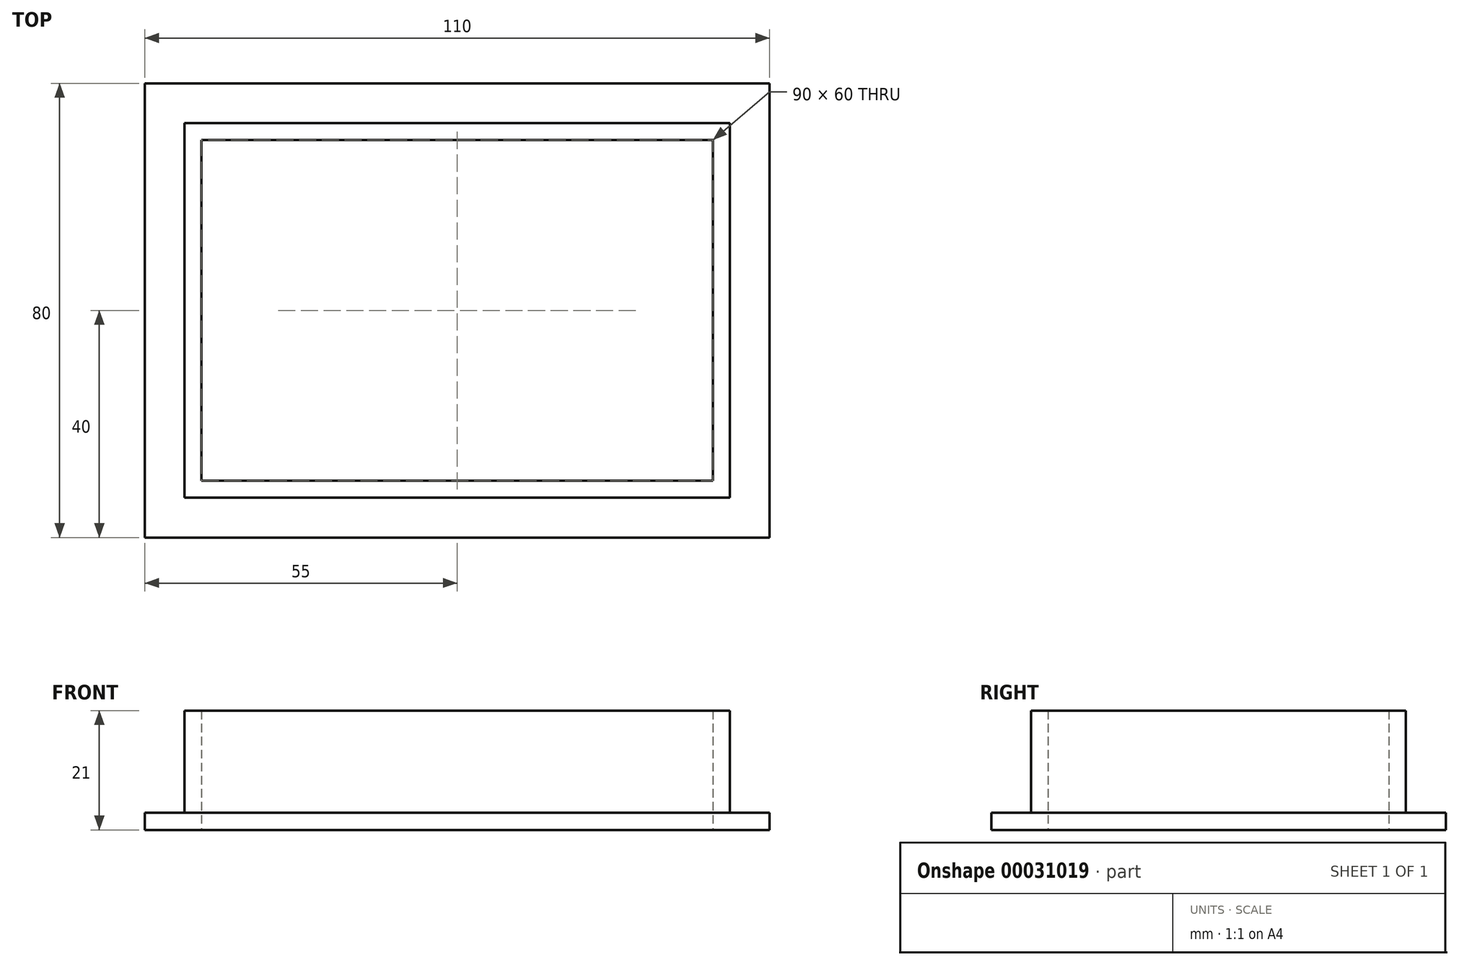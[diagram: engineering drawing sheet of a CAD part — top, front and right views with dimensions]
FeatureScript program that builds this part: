
annotation { "Feature Type Name" : "Feature", "Feature Type Description" : "" }
export const myFeature = defineFeature(function(context is Context, id is Id, definition is map)
    precondition{}
    {
        {
            var Q0;
            Q0=qCreatedBy(makeId("Top.planeOp"),FACE);
            var sketch = newSketch(context, id + "F0", { "sketchPlane" : qUnion([Q0])});
            skLineSegment(sketch, "E0.bottom", {"start": v(0, 0) * mm, "end": v(110, 0) * mm});
            skLineSegment(sketch, "E0.top", {"start": v(0, 80) * mm, "end": v(110, 80) * mm});
            skLineSegment(sketch, "E0.left", {"start": v(0, 0) * mm, "end": v(0, 80) * mm});
            skLineSegment(sketch, "E0.right", {"start": v(110, 0) * mm, "end": v(110, 80) * mm});
            skLineSegment(sketch, "E1.bottom", {"start": v(10, 10) * mm, "end": v(100, 10) * mm});
            skLineSegment(sketch, "E1.top", {"start": v(10, 70) * mm, "end": v(100, 70) * mm});
            skLineSegment(sketch, "E1.left", {"start": v(10, 10) * mm, "end": v(10, 70) * mm});
            skLineSegment(sketch, "E1.right", {"start": v(100, 10) * mm, "end": v(100, 70) * mm});
            skSolve(sketch);
        }
        {
            var Q0;
            Q0=makeQuery(id+"F0.imprint","IMPRINT",FACE,{"disambiguationData":[TD([[makeQuery(id+"F0.imprint","IMPRINT",EDGE,{"derivedFrom":sQuery(id+"F0.wireOp",EDGE,"E0.bottom")}),1.0]])]});
            extrude(context, id + "F1", {"entities" : qUnion([Q0]), "depth" : 3 * mm});
        }
        {
            var Q0;
            Q0=makeQuery(id+"F1.opExtrude","CAP_FACE",FACE,{"disambiguationData":[OSD([sQuery(id+"F0.wireOp",EDGE,"E0.bottom"),sQuery(id+"F0.wireOp",EDGE,"E0.top"),sQuery(id+"F0.wireOp",EDGE,"E0.left"),sQuery(id+"F0.wireOp",EDGE,"E0.right"),sQuery(id+"F0.wireOp",EDGE,"E1.bottom"),sQuery(id+"F0.wireOp",EDGE,"E1.top"),sQuery(id+"F0.wireOp",EDGE,"E1.left"),sQuery(id+"F0.wireOp",EDGE,"E1.right")])],"isStart":false});
            var sketch = newSketch(context, id + "F2", { "sketchPlane" : qUnion([Q0])});
            skLineSegment(sketch, "E2.bottom", {"start": v(7, 73) * mm, "end": v(103, 73) * mm});
            skLineSegment(sketch, "E2.top", {"start": v(7, 7) * mm, "end": v(103, 7) * mm});
            skLineSegment(sketch, "E2.left", {"start": v(7, 73) * mm, "end": v(7, 7) * mm});
            skLineSegment(sketch, "E2.right", {"start": v(103, 73) * mm, "end": v(103, 7) * mm});
            skSolve(sketch);
        }
        {
            var Q0;
            Q0=makeQuery(id+"F2.imprint","IMPRINT",FACE,{"disambiguationData":[TD([[makeQuery(id+"F2.imprint","IMPRINT",EDGE,{"derivedFrom":sQuery(id+"F2.wireOp",EDGE,"E2.bottom")}),-1.0]])]});
            extrude(context, id + "F3", {"entities" : qUnion([Q0]), "operationType" : NewBodyOperationType.ADD, "depth" : 18 * mm});
        }
    });
